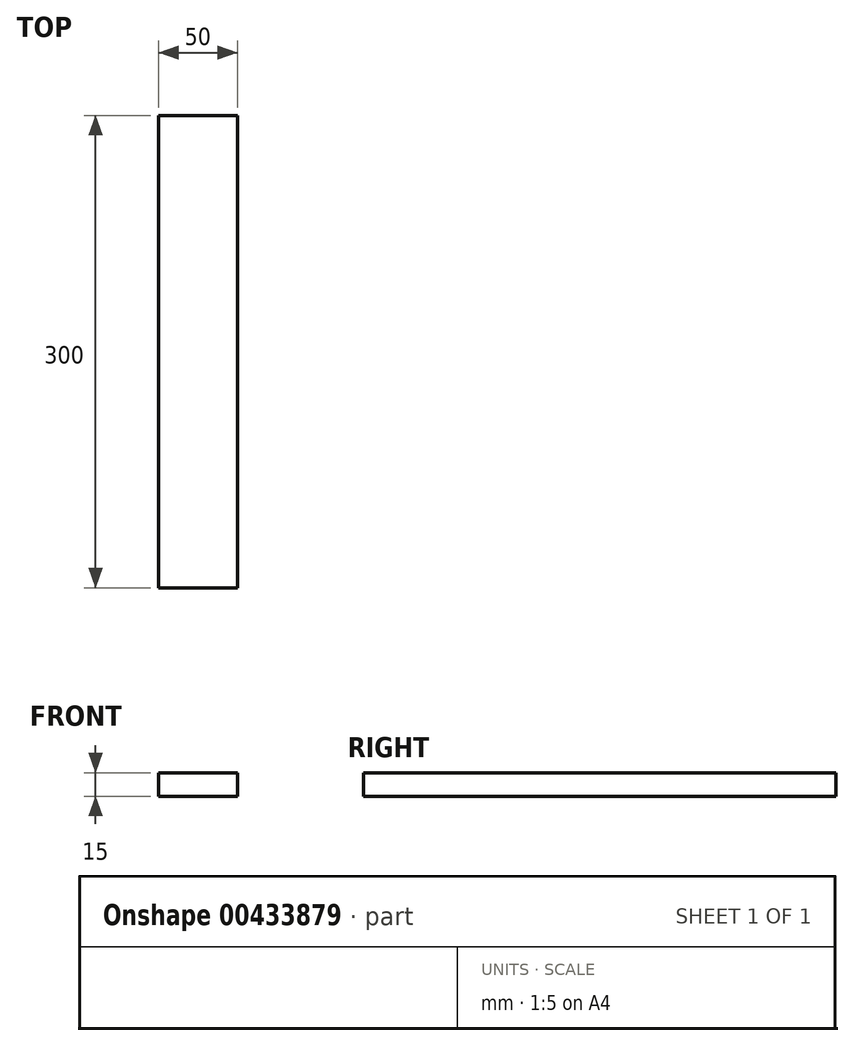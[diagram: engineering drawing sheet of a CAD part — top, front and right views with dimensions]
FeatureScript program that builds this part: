
annotation { "Feature Type Name" : "Feature", "Feature Type Description" : "" }
export const myFeature = defineFeature(function(context is Context, id is Id, definition is map)
    precondition{}
    {
        {
            var Q0;
            Q0=qCreatedBy(makeId("Front.planeOp"),FACE);
            var sketch = newSketch(context, id + "F0", { "sketchPlane" : qUnion([Q0])});
            skLineSegment(sketch, "E0.bottom", {"start": v(-26.9, 45) * mm, "end": v(23.1, 45) * mm});
            skLineSegment(sketch, "E0.top", {"start": v(-26.9, 30) * mm, "end": v(23.1, 30) * mm});
            skLineSegment(sketch, "E0.left", {"start": v(-26.9, 45) * mm, "end": v(-26.9, 30) * mm});
            skLineSegment(sketch, "E0.right", {"start": v(23.1, 45) * mm, "end": v(23.1, 30) * mm});
            skSolve(sketch);
        }
        {
            var Q0;
            Q0=makeQuery(id+"F0.imprint","IMPRINT",FACE,{"disambiguationData":[TD([[makeQuery(id+"F0.imprint","IMPRINT",EDGE,{"derivedFrom":sQuery(id+"F0.wireOp",EDGE,"E0.bottom")}),-1.0]])]});
            extrude(context, id + "F1", {"entities" : qUnion([Q0]), "depth" : 300 * mm});
        }
    });
